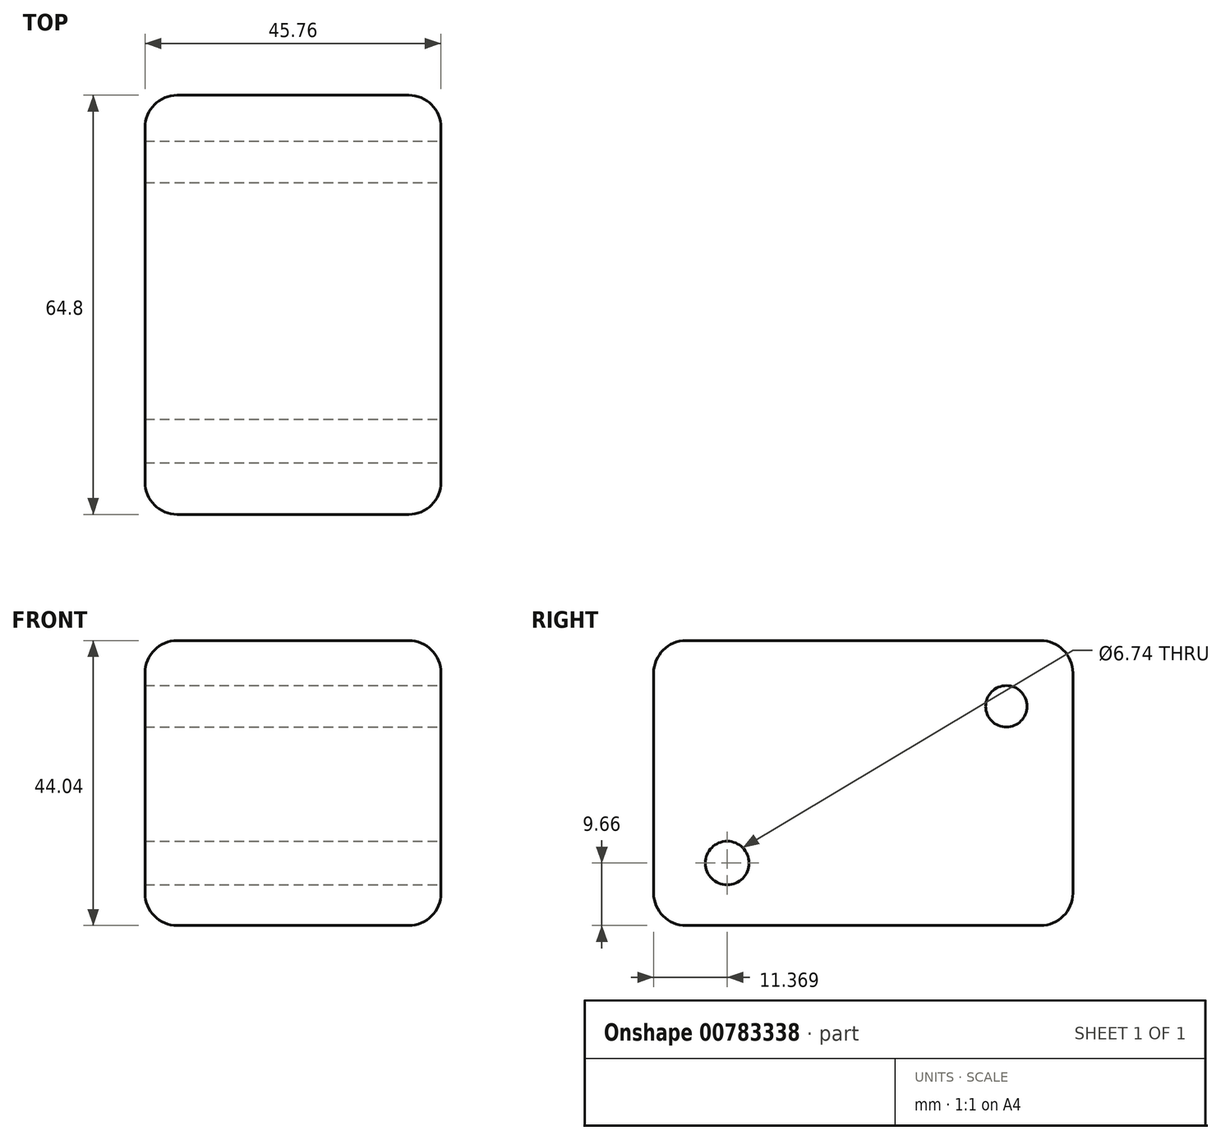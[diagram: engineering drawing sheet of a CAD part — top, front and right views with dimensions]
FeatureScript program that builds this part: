
annotation { "Feature Type Name" : "Feature", "Feature Type Description" : "" }
export const myFeature = defineFeature(function(context is Context, id is Id, definition is map)
    precondition{}
    {
        {
            var Q0;
            Q0=qCreatedBy(makeId("Front.planeOp"),FACE);
            var sketch = newSketch(context, id + "F0", { "sketchPlane" : qUnion([Q0])});
            skLineSegment(sketch, "E0.bottom", {"start": v(-22.88, -22.02) * mm, "end": v(22.88, -22.02) * mm});
            skLineSegment(sketch, "E0.top", {"start": v(-22.88, 22.02) * mm, "end": v(22.88, 22.02) * mm});
            skLineSegment(sketch, "E0.left", {"start": v(-22.88, -22.02) * mm, "end": v(-22.88, 22.02) * mm});
            skLineSegment(sketch, "E0.right", {"start": v(22.88, -22.02) * mm, "end": v(22.88, 22.02) * mm});
            skPoint(sketch, "E0.middle", {"position": v(0, 0) * mm});
            skSolve(sketch);
        }
        {
            var Q0;
            Q0 = qSketchRegion(id + "F0", true);
            extrude(context, id + "F1", {"entities" : qUnion([Q0]), "depth" : 64.8 * mm, "offsetDistance" : 25 * mm});
        }
        {
            var Q0;
            Q0=makeQuery(id+"F1.opExtrude","SWEPT_FACE",FACE,{"disambiguationData":[OSD([sQuery(id+"F0.wireOp",EDGE,"E0.top")])]});
            var Q1;
            Q1=makeQuery(id+"F1.opExtrude","SWEPT_FACE",FACE,{"disambiguationData":[OSD([sQuery(id+"F0.wireOp",EDGE,"E0.right")])]});
            var Q2;
            Q2=makeQuery(id+"F1.opExtrude","SWEPT_FACE",FACE,{"disambiguationData":[OSD([sQuery(id+"F0.wireOp",EDGE,"E0.left")])]});
            var Q3;
            Q3=makeQuery(id+"F1.opExtrude","SWEPT_FACE",FACE,{"disambiguationData":[OSD([sQuery(id+"F0.wireOp",EDGE,"E0.bottom")])]});
            fillet(context, id + "F2", {"entities" : qUnion([Q0, Q1, Q2, Q3]), "radius" : 5 * mm, "tangentPropagation" : true, "allowEdgeOverflow" : false});
        }
        {
            var Q0;
            Q0=makeQuery(id+"F1.opExtrude","SWEPT_FACE",FACE,{"disambiguationData":[OSD([sQuery(id+"F0.wireOp",EDGE,"E0.right")])]});
            var sketch = newSketch(context, id + "F3", { "sketchPlane" : qUnion([Q0])});
            skCircle(sketch, "E1", {"center": v(-10.28, 11.86) * mm, "radius": 3.2 * mm});
            skCircle(sketch, "E2", {"center": v(-53.43, -12.36) * mm, "radius": 3.37 * mm});
            skSolve(sketch);
        }
        {
            var Q0;
            Q0 = qSketchRegion(id + "F3", true);
            extrude(context, id + "F4", {"entities" : qUnion([Q0]), "operationType" : NewBodyOperationType.REMOVE, "oppositeDirection" : true, "depth" : 124.6 * mm, "offsetDistance" : 25 * mm});
        }
    });
